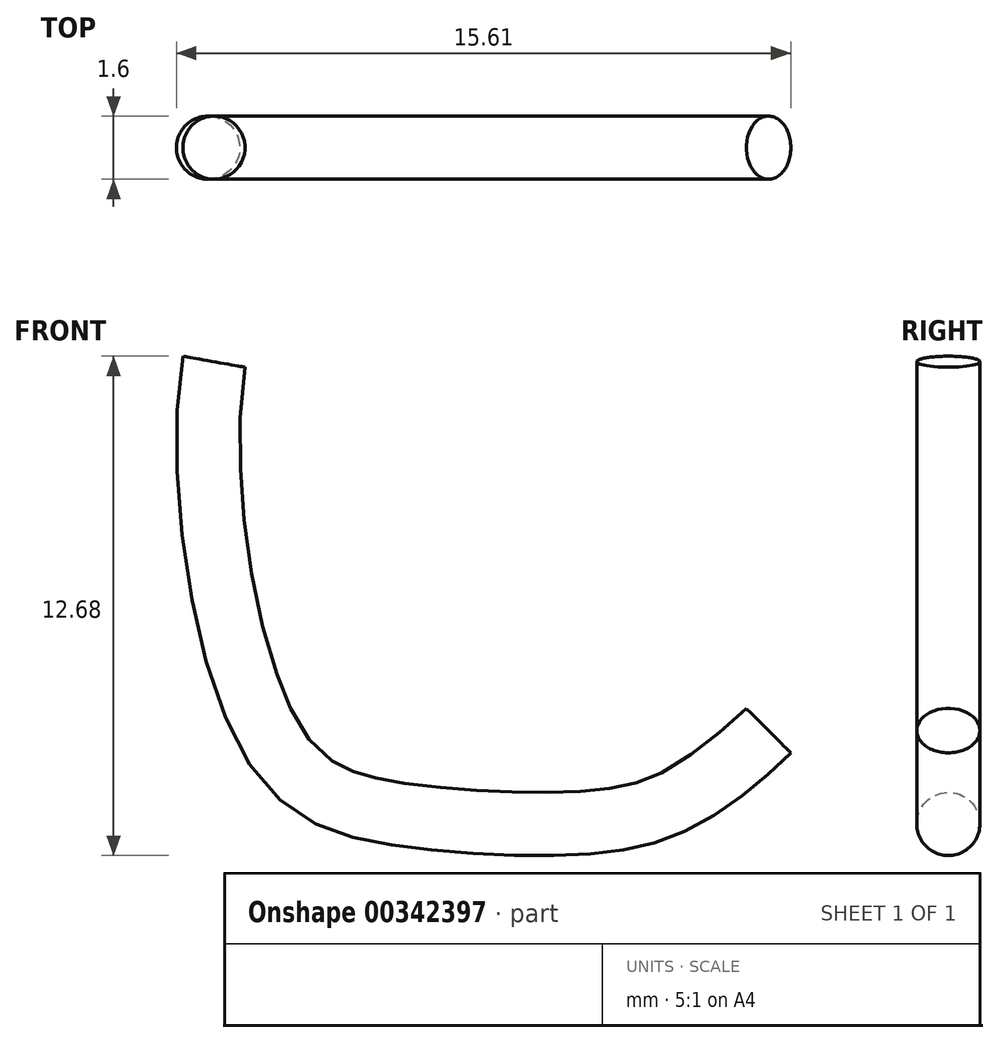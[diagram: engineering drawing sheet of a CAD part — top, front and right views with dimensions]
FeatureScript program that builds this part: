
annotation { "Feature Type Name" : "Feature", "Feature Type Description" : "" }
export const myFeature = defineFeature(function(context is Context, id is Id, definition is map)
    precondition{}
    {
        {
            var Q0;
            Q0=qCreatedBy(makeId("Front.planeOp"),FACE);
            var sketch = newSketch(context, id + "F0", { "sketchPlane" : qUnion([Q0])});
            skFitSpline(sketch, "E0", {"points": [v(-5.96, 0) * mm, v(-4.46, -9.65) * mm, v(-1.28, -11.48) * mm, v(3.36, -11.7) * mm, v(5.81, -11.12) * mm, v(8.12, -9.36) * mm], "startDerivative": vector(-4.64, -26.25) * mm, "endDerivative": vector(11.49, 11.49) * mm});
            skSolve(sketch);
        }
        {
            var Q0;
            Q0=sQuery(id+"F0.wireOp",VERTEX,"E0.start");
            var Q1;
            Q1=sQuery(id+"F0.wireOp",EDGE,"E0");
            cPlane(context, id + "F1", {"entities" : qUnion([Q0, Q1]), "cplaneType" : CPlaneType.CURVE_POINT, "offset" : 25.4 * mm, "width" : 152.4 * mm, "height" : 152.4 * mm});
        }
        {
            var Q0;
            Q0=qCreatedBy(id+"F1.planeOp",FACE);
            var sketch = newSketch(context, id + "F2", { "sketchPlane" : qUnion([Q0])});
            skCircle(sketch, "E1", {"center": v(-5.88, 0) * mm, "radius": 0.8 * mm});
            skSolve(sketch);
        }
        {
            var Q0;
            Q0 = qSketchRegion(id + "F2", true);
            var Q1;
            Q1 = qConstructionFilter(qBodyType(qCreatedBy(id + "F0" ,EDGE), BodyType.WIRE), ConstructionObject.NO);
            sweep(context, id + "F3", {"profiles" : qUnion([Q0]), "path" : qUnion([Q1])});
        }
    });
